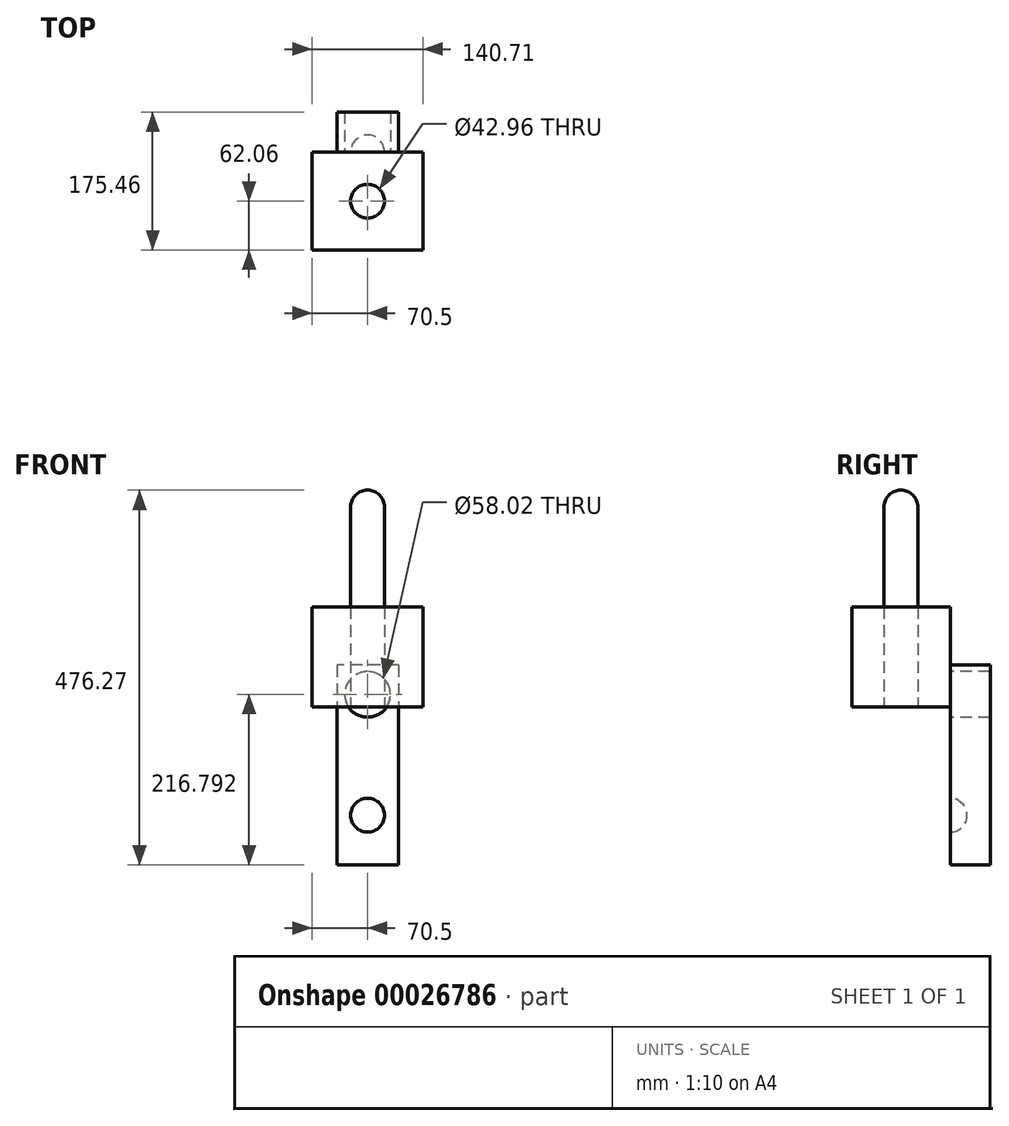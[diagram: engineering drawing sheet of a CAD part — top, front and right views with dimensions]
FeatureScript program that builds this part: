
annotation { "Feature Type Name" : "Feature", "Feature Type Description" : "" }
export const myFeature = defineFeature(function(context is Context, id is Id, definition is map)
    precondition{}
    {
        {
            var Q0;
            Q0=qCreatedBy(makeId("Top.planeOp"),FACE);
            var sketch = newSketch(context, id + "F0", { "sketchPlane" : qUnion([Q0])});
            skLineSegment(sketch, "E0.bottom", {"start": v(-70.5, 62.6) * mm, "end": v(70.21, 62.6) * mm});
            skLineSegment(sketch, "E0.top", {"start": v(-70.5, -62.06) * mm, "end": v(70.21, -62.06) * mm});
            skLineSegment(sketch, "E0.left", {"start": v(-70.5, 62.6) * mm, "end": v(-70.5, -62.06) * mm});
            skLineSegment(sketch, "E0.right", {"start": v(70.21, 62.6) * mm, "end": v(70.21, -62.06) * mm});
            skCircle(sketch, "E1", {"center": v(0, 0) * mm, "radius": 21.48 * mm});
            skSolve(sketch);
        }
        {
            var Q0;
            Q0 = qSketchRegion(id + "F0", true);
            extrude(context, id + "F1", {"entities" : qUnion([Q0]), "depth" : 127 * mm});
        }
        {
            var Q0;
            Q0=makeQuery(id+"F1.opExtrude","CAP_FACE",FACE,{"disambiguationData":[OSD([sQuery(id+"F0.wireOp",EDGE,"E0.bottom"),sQuery(id+"F0.wireOp",EDGE,"E0.top"),sQuery(id+"F0.wireOp",EDGE,"E0.left"),sQuery(id+"F0.wireOp",EDGE,"E0.right"),sQuery(id+"F0.wireOp",EDGE,"E1")])],"isStart":false});
            var sketch = newSketch(context, id + "F2", { "sketchPlane" : qUnion([Q0])});
            skSolve(sketch);
        }
        {
            var Q0;
            Q0=makeQuery(id+"F2.imprint","IMPRINT",FACE,{"disambiguationData":[TD([[makeQuery(id+"F2.imprint","IMPRINT",EDGE,{"derivedFrom":makeQuery(id+"F1.opExtrude","CAP_EDGE",EDGE,{"disambiguationData":[OSD([sQuery(id+"F0.wireOp",EDGE,"E1")])],"isStart":false})}),1.0]])]});
            extrude(context, id + "F3", {"entities" : qUnion([Q0]), "depth" : 127 * mm});
        }
        {
            var Q0;
            Q0=makeQuery(id+"F3.opExtrude","CAP_FACE",FACE,{"disambiguationData":[OSD([sQuery(id+"F0.wireOp",EDGE,"E1")])],"isStart":false});
            var sketch = newSketch(context, id + "F4", { "sketchPlane" : qUnion([Q0])});
            skLineSegment(sketch, "E2", {"start": v(0, 21.48) * mm, "end": v(0, -21.48) * mm});
            skSolve(sketch);
        }
        {
            var Q0;
            {var subQ1=sQuery(id+"F4.wireOp",EDGE,"E2");Q0=makeQuery(id+"F4.imprint","IMPRINT",FACE,{"disambiguationData":[TD([[makeQuery(id+"F4.imprint","IMPRINT",EDGE,{"derivedFrom":subQ1}),1.0]])]});}
            var Q1;
            Q1=sQuery(id+"F4.wireOp",EDGE,"E2");
            revolve(context, id + "F5", {"operationType" : NewBodyOperationType.ADD, "entities" : qUnion([Q0]), "axis" : qUnion([Q1]), "revolveType" : RevolveType.FULL});
        }
        {
            var Q0;
            Q0=makeQuery(id+"F1.opExtrude","SWEPT_FACE",FACE,{"disambiguationData":[OSD([sQuery(id+"F0.wireOp",EDGE,"E0.bottom")])]});
            var sketch = newSketch(context, id + "F6", { "sketchPlane" : qUnion([Q0])});
            skLineSegment(sketch, "E3.bottom", {"start": v(-39.3, 53.2) * mm, "end": v(39, 53.2) * mm});
            skLineSegment(sketch, "E3.top", {"start": v(-39.3, -200.8) * mm, "end": v(39, -200.8) * mm});
            skLineSegment(sketch, "E3.left", {"start": v(-39.3, 53.2) * mm, "end": v(-39.3, -200.8) * mm});
            skLineSegment(sketch, "E3.right", {"start": v(39, 53.2) * mm, "end": v(39, -200.8) * mm});
            skCircle(sketch, "E4", {"center": v(0, 16) * mm, "radius": 29 * mm});
            skSolve(sketch);
        }
        {
            var Q0;
            {var subQ5=sQuery(id+"F6.wireOp",EDGE,"E3.bottom");Q0=makeQuery(id+"F6.imprint","IMPRINT",FACE,{"disambiguationData":[TD([[makeQuery(id+"F6.imprint","IMPRINT",EDGE,{"derivedFrom":subQ5}),-1.0]])]});}
            var Q1;
            {var subQ0=sQuery(id+"F0.wireOp",EDGE,"E0.bottom");var subQ1=makeQuery(id+"F1.opExtrude","CAP_EDGE",EDGE,{"disambiguationData":[OSD([subQ0])],"isStart":false});var subQ4=sQuery(id+"F6.wireOp",EDGE,"E3.left");var subQ5=makeQuery(id+"F6.imprint","INTERSECT",VERTEX,{"derivedFrom":[subQ1,subQ4]});Q1=makeQuery(id+"F6.imprint","IMPRINT",FACE,{"disambiguationData":[TD([[makeQuery(id+"F6.imprint","IMPRINT",EDGE,{"disambiguationData":[TD([[subQ5,-1.0]])],"derivedFrom":subQ4}),1.0]])]});}
            var Q2;
            {var subQ5=sQuery(id+"F6.wireOp",EDGE,"E3.top");Q2=makeQuery(id+"F6.imprint","IMPRINT",FACE,{"disambiguationData":[TD([[makeQuery(id+"F6.imprint","IMPRINT",EDGE,{"derivedFrom":subQ5}),1.0]])]});}
            extrude(context, id + "F7", {"entities" : qUnion([Q0, Q1, Q2]), "depth" : 50.8 * mm});
        }
        {
            var Q0;
            Q0=makeQuery(id+"F7.opExtrude","CAP_FACE",FACE,{"disambiguationData":[OSD([sQuery(id+"F6.wireOp",EDGE,"E3.bottom"),sQuery(id+"F6.wireOp",EDGE,"E3.top"),sQuery(id+"F6.wireOp",EDGE,"E3.left"),sQuery(id+"F6.wireOp",EDGE,"E3.right")])],"isStart":true});
            var sketch = newSketch(context, id + "F8", { "sketchPlane" : qUnion([Q0])});
            skArc(sketch, "E5", {"start": v(0, -158.95) * mm, "mid": v(21.48, -137.47) * mm, "end": v(0, -116) * mm});
            skLineSegment(sketch, "E6", {"start": v(0, -116) * mm, "end": v(0, -158.95) * mm});
            skSolve(sketch);
        }
        {
            var Q0;
            Q0=makeQuery(id+"F8.imprint","IMPRINT",FACE,{"disambiguationData":[TD([[makeQuery(id+"F8.imprint","IMPRINT",EDGE,{"derivedFrom":sQuery(id+"F8.wireOp",EDGE,"E5")}),1.0]])]});
            var Q1;
            Q1=sQuery(id+"F8.wireOp",EDGE,"E6");
            revolve(context, id + "F9", {"operationType" : NewBodyOperationType.REMOVE, "entities" : qUnion([Q0]), "axis" : qUnion([Q1]), "revolveType" : RevolveType.FULL, "oppositeDirection" : true});
        }
    });
